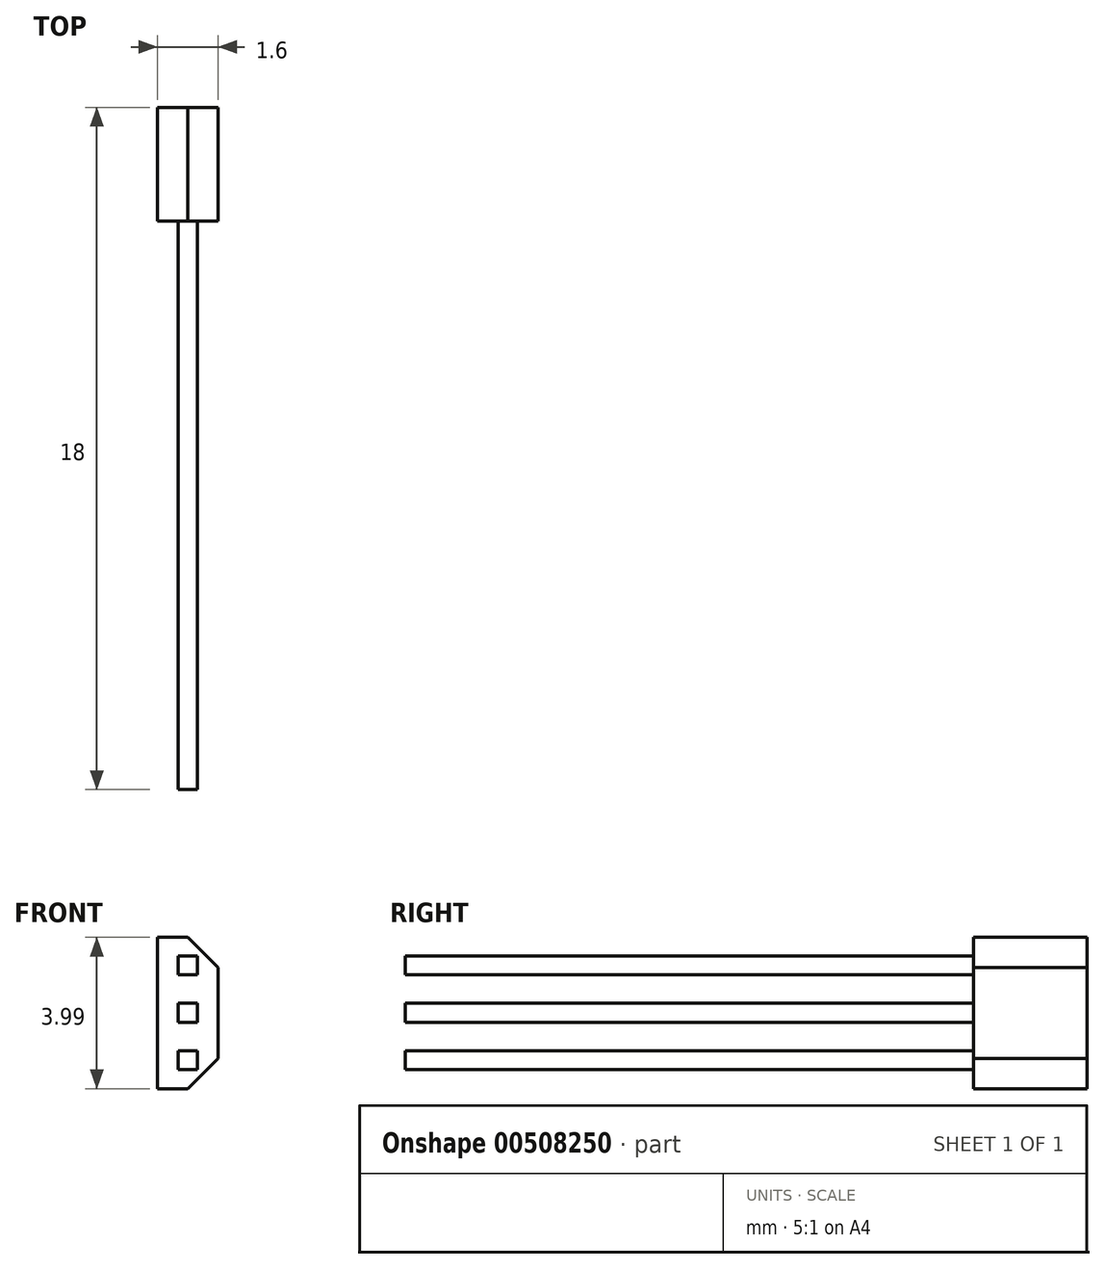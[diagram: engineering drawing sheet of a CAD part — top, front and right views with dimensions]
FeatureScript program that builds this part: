
annotation { "Feature Type Name" : "Feature", "Feature Type Description" : "" }
export const myFeature = defineFeature(function(context is Context, id is Id, definition is map)
    precondition{}
    {
        {
            var Q0;
            Q0=qCreatedBy(makeId("Front.planeOp"),FACE);
            var sketch = newSketch(context, id + "F0", { "sketchPlane" : qUnion([Q0])});
            skLineSegment(sketch, "E0.bottom", {"start": v(-0.25, 1) * mm, "end": v(0.25, 1) * mm});
            skLineSegment(sketch, "E0.top", {"start": v(-0.25, 0.5) * mm, "end": v(0.25, 0.5) * mm});
            skLineSegment(sketch, "E0.left", {"start": v(-0.25, 1) * mm, "end": v(-0.25, 0.5) * mm});
            skLineSegment(sketch, "E0.right", {"start": v(0.25, 1) * mm, "end": v(0.25, 0.5) * mm});
            skLineSegment(sketch, "E1.1.0.0", {"start": v(-0.25, 2.25) * mm, "end": v(0.25, 2.25) * mm});
            skLineSegment(sketch, "E1.1.0.1", {"start": v(0.25, 2.25) * mm, "end": v(0.25, 1.75) * mm});
            skLineSegment(sketch, "E1.1.0.2", {"start": v(-0.25, 1.75) * mm, "end": v(0.25, 1.75) * mm});
            skLineSegment(sketch, "E1.1.0.3", {"start": v(-0.25, 2.25) * mm, "end": v(-0.25, 1.75) * mm});
            skLineSegment(sketch, "E1.2.0.0", {"start": v(-0.25, 3.5) * mm, "end": v(0.25, 3.5) * mm});
            skLineSegment(sketch, "E1.2.0.1", {"start": v(0.25, 3.5) * mm, "end": v(0.25, 3) * mm});
            skLineSegment(sketch, "E1.2.0.2", {"start": v(-0.25, 3) * mm, "end": v(0.25, 3) * mm});
            skLineSegment(sketch, "E1.2.0.3", {"start": v(-0.25, 3.5) * mm, "end": v(-0.25, 3) * mm});
            skLineSegment(sketch, "E1.direction1", {"start": v(-0.25, 1) * mm, "end": v(-0.25, 2.25) * mm, "construction": true});
            skLineSegment(sketch, "E2.bottom", {"start": v(0, 0) * mm, "end": v(-0.8, 0) * mm});
            skLineSegment(sketch, "E2.top", {"start": v(0, 4) * mm, "end": v(-0.8, 4) * mm});
            skLineSegment(sketch, "E2.left", {"start": v(0.8, 0.8) * mm, "end": v(0.8, 3.2) * mm});
            skLineSegment(sketch, "E2.right", {"start": v(-0.8, 0) * mm, "end": v(-0.8, 4) * mm});
            skLineSegment(sketch, "E3", {"start": v(0, 4) * mm, "end": v(0.8, 3.2) * mm});
            skLineSegment(sketch, "E4", {"start": v(0, 0) * mm, "end": v(0.8, 0.8) * mm});
            skPoint(sketch, "E5.orphan", {"position": v(0.8, 0) * mm});
            skSolve(sketch);
        }
        {
            var Q0;
            Q0=makeQuery(id+"F0.imprint","IMPRINT",FACE,{"disambiguationData":[TD([[makeQuery(id+"F0.imprint","IMPRINT",EDGE,{"derivedFrom":sQuery(id+"F0.wireOp",EDGE,"E0.bottom")}),1.0]])]});
            extrude(context, id + "F1", {"entities" : qUnion([Q0]), "depth" : 3 * mm});
        }
        {
            var Q0;
            Q0=makeQuery(id+"F0.imprint","IMPRINT",FACE,{"disambiguationData":[TD([[makeQuery(id+"F0.imprint","IMPRINT",EDGE,{"derivedFrom":sQuery(id+"F0.wireOp",EDGE,"E1.2.0.0")}),-1.0]])]});
            var Q1;
            Q1=makeQuery(id+"F0.imprint","IMPRINT",FACE,{"disambiguationData":[TD([[makeQuery(id+"F0.imprint","IMPRINT",EDGE,{"derivedFrom":sQuery(id+"F0.wireOp",EDGE,"E1.1.0.0")}),-1.0]])]});
            var Q2;
            Q2=makeQuery(id+"F0.imprint","IMPRINT",FACE,{"disambiguationData":[TD([[makeQuery(id+"F0.imprint","IMPRINT",EDGE,{"derivedFrom":sQuery(id+"F0.wireOp",EDGE,"E0.bottom")}),-1.0]])]});
            extrude(context, id + "F2", {"entities" : qUnion([Q0, Q1, Q2]), "operationType" : NewBodyOperationType.ADD, "depth" : 18 * mm});
        }
    });
